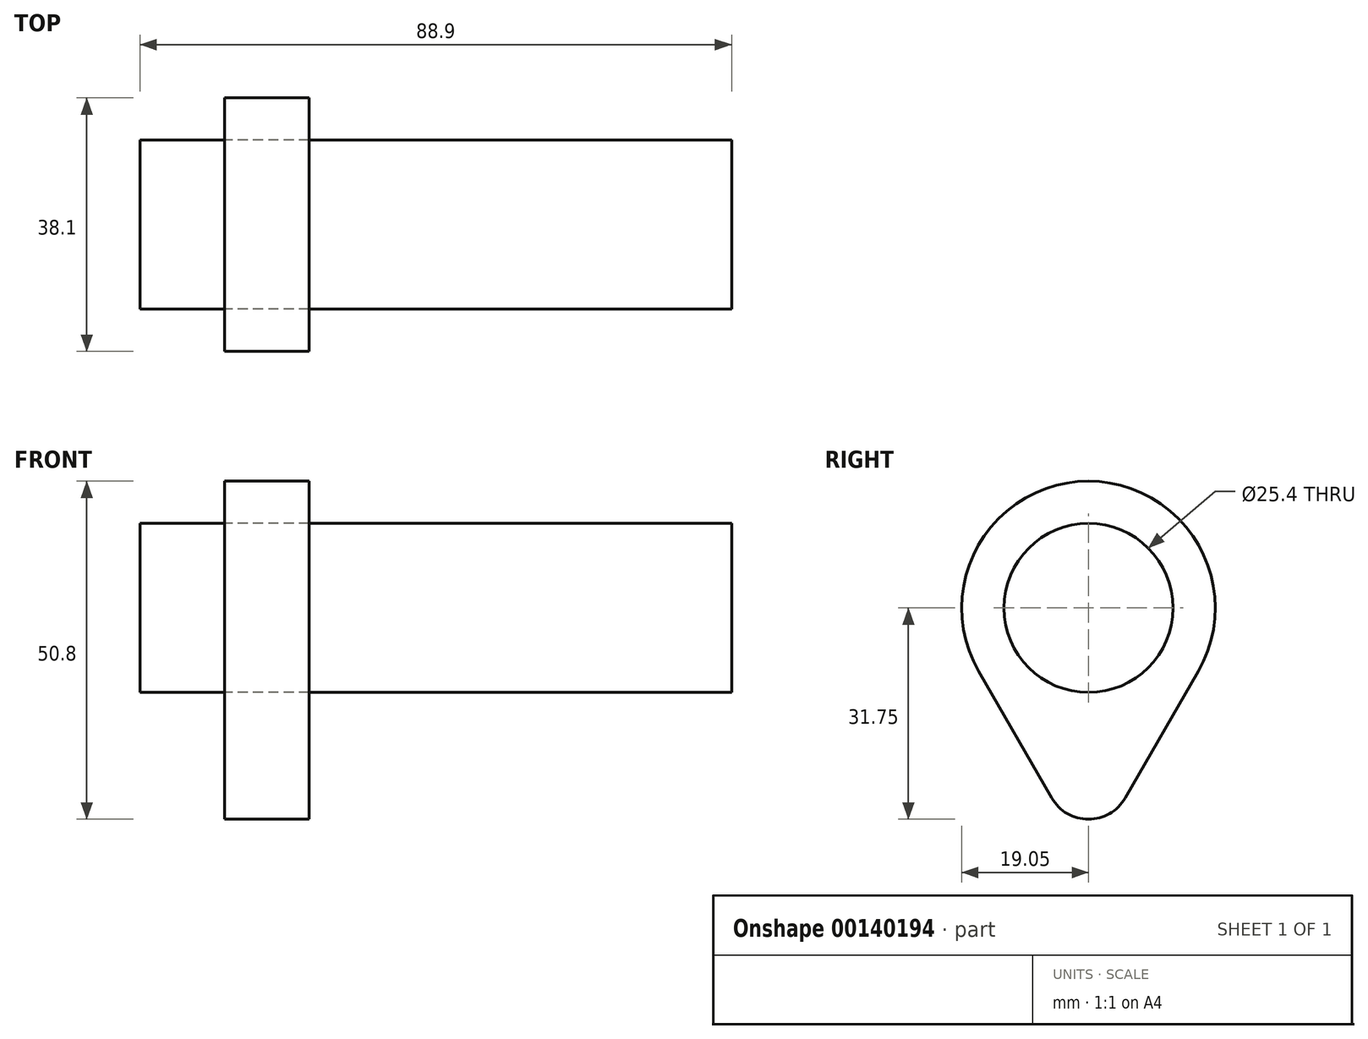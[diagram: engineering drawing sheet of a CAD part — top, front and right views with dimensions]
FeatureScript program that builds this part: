
annotation { "Feature Type Name" : "Feature", "Feature Type Description" : "" }
export const myFeature = defineFeature(function(context is Context, id is Id, definition is map)
    precondition{}
    {
        {
            var Q0;
            Q0=qCreatedBy(makeId("Right.planeOp"),FACE);
            var sketch = newSketch(context, id + "F0", { "sketchPlane" : qUnion([Q0])});
            skCircle(sketch, "E0", {"center": v(0, 0) * mm, "radius": 12.7 * mm});
            skArc(sketch, "E1", {"start": v(16.5, -9.52) * mm, "mid": v(0, 19.05) * mm, "end": v(-16.5, -9.53) * mm});
            skArc(sketch, "E2", {"start": v(-5.5, -28.57) * mm, "mid": v(0, -31.75) * mm, "end": v(5.5, -28.58) * mm});
            skLineSegment(sketch, "E3", {"start": v(-16.5, -9.53) * mm, "end": v(-5.5, -28.57) * mm});
            skLineSegment(sketch, "E4", {"start": v(17.38, -8) * mm, "end": v(5.5, -28.58) * mm});
            skSolve(sketch);
        }
        {
            var Q0;
            Q0=makeQuery(id+"F0.imprint","IMPRINT",FACE,{"disambiguationData":[TD([[makeQuery(id+"F0.imprint","IMPRINT",EDGE,{"derivedFrom":sQuery(id+"F0.wireOp",EDGE,"E0")}),1.0]])]});
            extrude(context, id + "F1", {"entities" : qUnion([Q0]), "depth" : 76.2 * mm, "hasSecondDirection" : true, "secondDirectionOppositeDirection" : true, "secondDirectionDepth" : 12.7 * mm});
        }
        {
            var Q0;
            Q0=makeQuery(id+"F0.imprint","IMPRINT",FACE,{"disambiguationData":[TD([[makeQuery(id+"F0.imprint","IMPRINT",EDGE,{"derivedFrom":sQuery(id+"F0.wireOp",EDGE,"E0")}),-1.0]])]});
            extrude(context, id + "F2", {"entities" : qUnion([Q0]), "depth" : 12.7 * mm});
        }
    });
